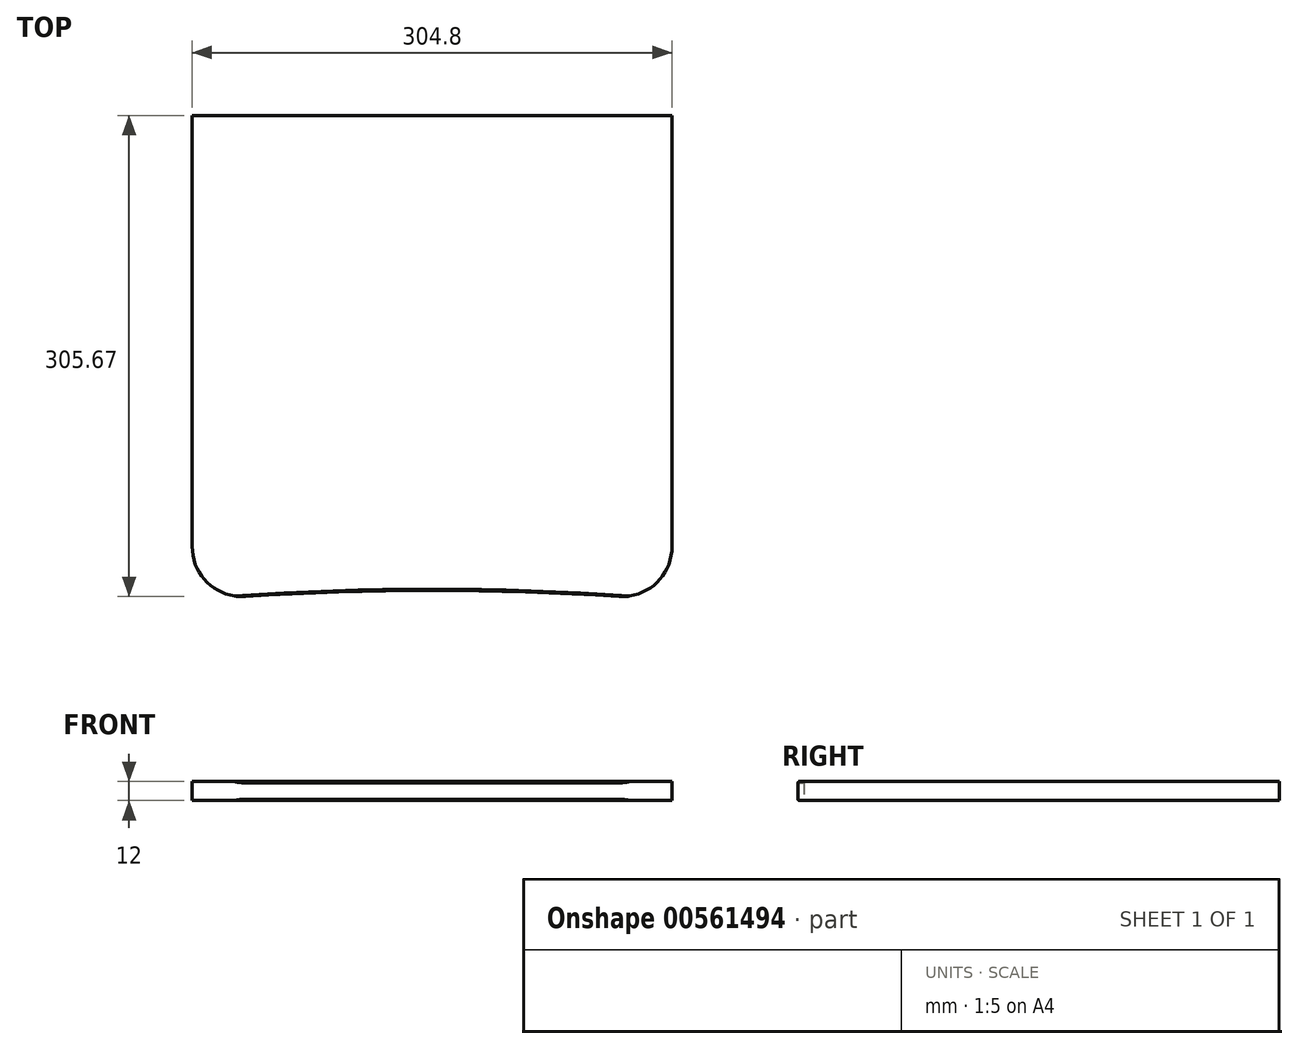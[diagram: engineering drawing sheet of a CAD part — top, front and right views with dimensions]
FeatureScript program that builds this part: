
annotation { "Feature Type Name" : "Feature", "Feature Type Description" : "" }
export const myFeature = defineFeature(function(context is Context, id is Id, definition is map)
    precondition{}
    {
        {
            var Q0;
            Q0=qCreatedBy(makeId("Top.planeOp"),FACE);
            var sketch = newSketch(context, id + "F0", { "sketchPlane" : qUnion([Q0])});
            skLineSegment(sketch, "E0", {"start": v(-152.4, 150.88) * mm, "end": v(-152.4, -123.03) * mm});
            skArc(sketch, "E1", {"start": v(-152.4, -123.03) * mm, "mid": v(-142.36, -146.2) * mm, "end": v(-118.6, -154.72) * mm});
            skArc(sketch, "E2", {"start": v(-118.6, -154.72) * mm, "mid": v(0, -150.88) * mm, "end": v(118.6, -154.72) * mm});
            skArc(sketch, "E3", {"start": v(118.6, -154.72) * mm, "mid": v(142.36, -146.2) * mm, "end": v(152.4, -123.03) * mm});
            skLineSegment(sketch, "E4", {"start": v(152.4, -123.03) * mm, "end": v(152.4, 150.88) * mm});
            skLineSegment(sketch, "E5", {"start": v(-152.4, 150.88) * mm, "end": v(152.4, 150.88) * mm});
            skLineSegment(sketch, "E6", {"start": v(0, 150.88) * mm, "end": v(0, -150.88) * mm, "construction": true});
            skSolve(sketch);
        }
        {
            var Q0;
            Q0 = qSketchRegion(id + "F0", true);
            extrude(context, id + "F1", {"entities" : qUnion([Q0]), "depth" : 12 * mm, "offsetDistance" : 25.4 * mm});
        }
        {
            var Q0;
            Q0=makeQuery(id+"F1.opExtrude","CAP_EDGE",EDGE,{"disambiguationData":[OSD([sQuery(id+"F0.wireOp",EDGE,"E2")])],"isStart":false});
            var Q1;
            Q1=makeQuery(id+"F1.opExtrude","CAP_EDGE",EDGE,{"disambiguationData":[OSD([sQuery(id+"F0.wireOp",EDGE,"E2")])],"isStart":true});
            chamfer(context, id + "F2", {"entities" : qUnion([Q0, Q1]), "width" : 0.76 * mm});
        }
    });
